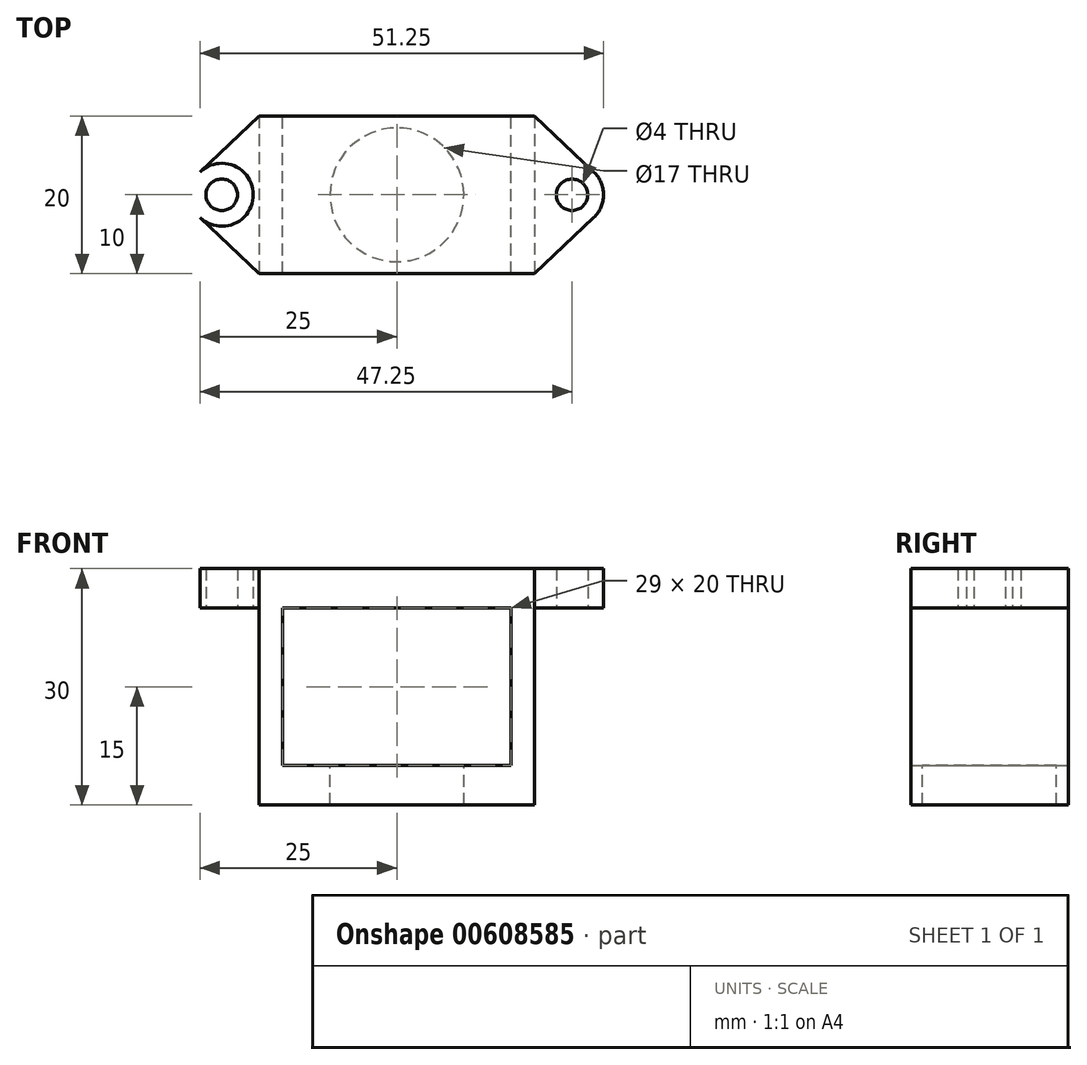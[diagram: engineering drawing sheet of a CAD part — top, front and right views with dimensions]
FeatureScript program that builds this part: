
annotation { "Feature Type Name" : "Feature", "Feature Type Description" : "" }
export const myFeature = defineFeature(function(context is Context, id is Id, definition is map)
    precondition{}
    {
        {
            var Q0;
            Q0=qCreatedBy(makeId("Top.planeOp"),FACE);
            var sketch = newSketch(context, id + "F0", { "sketchPlane" : qUnion([Q0])});
            skLineSegment(sketch, "E0", {"start": v(-22.25, 0) * mm, "end": v(22.25, 0) * mm, "construction": true});
            skCircle(sketch, "E1", {"center": v(22.25, 0) * mm, "radius": 2 * mm});
            skPoint(sketch, "E2", {"position": v(0, 0) * mm});
            skLineSegment(sketch, "E3.bottom", {"start": v(-17.5, 10) * mm, "end": v(17.5, 10) * mm});
            skLineSegment(sketch, "E3.top", {"start": v(-17.5, -10) * mm, "end": v(17.5, -10) * mm});
            skLineSegment(sketch, "E3.left", {"start": v(-17.5, 10) * mm, "end": v(-17.5, -10) * mm});
            skLineSegment(sketch, "E3.right", {"start": v(17.5, 10) * mm, "end": v(17.5, -10) * mm});
            skCircle(sketch, "E4", {"center": v(22.25, 0) * mm, "radius": 4 * mm});
            skLineSegment(sketch, "E5", {"start": v(17.5, -10) * mm, "end": v(25, -2.9) * mm});
            skLineSegment(sketch, "E6", {"start": v(17.5, 10) * mm, "end": v(25, 2.9) * mm});
            skLineSegment(sketch, "E7", {"start": v(0, 0) * mm, "end": v(0, 5.6) * mm, "construction": true});
            skLineSegment(sketch, "E8.MirrorCS", {"start": v(-17.5, 10) * mm, "end": v(-25, 2.9) * mm});
            skCircle(sketch, "E9.MirrorC", {"center": v(-22.25, 0) * mm, "radius": 2 * mm});
            skCircle(sketch, "E10.MirrorC", {"center": v(-22.25, 0) * mm, "radius": 4 * mm});
            skLineSegment(sketch, "E11.MirrorCS", {"start": v(-17.5, -10) * mm, "end": v(-25, -2.9) * mm});
            skLineSegment(sketch, "E12", {"start": v(14.5, -10) * mm, "end": v(14.5, 10) * mm});
            skLineSegment(sketch, "E13.MirrorCS", {"start": v(-14.5, -10) * mm, "end": v(-14.5, 10) * mm});
            skSolve(sketch);
        }
        {
            var Q0;
            Q0=makeQuery(id+"F0.imprint","IMPRINT",FACE,{"disambiguationData":[TD([[makeQuery(id+"F0.imprint","IMPRINT",EDGE,{"derivedFrom":sQuery(id+"F0.wireOp",EDGE,"E3.left")}),-1.0]])]});
            var Q1;
            Q1=makeQuery(id+"F0.imprint","IMPRINT",FACE,{"disambiguationData":[TD([[makeQuery(id+"F0.imprint","IMPRINT",EDGE,{"derivedFrom":sQuery(id+"F0.wireOp",EDGE,"E9.MirrorC")}),1.0]])]});
            var Q2;
            Q2=makeQuery(id+"F0.imprint","IMPRINT",FACE,{"disambiguationData":[TD([[makeQuery(id+"F0.imprint","IMPRINT",EDGE,{"derivedFrom":sQuery(id+"F0.wireOp",EDGE,"E3.bottom")}),-1.0]])]});
            var Q3;
            Q3=makeQuery(id+"F0.imprint","IMPRINT",FACE,{"disambiguationData":[TD([[makeQuery(id+"F0.imprint","IMPRINT",EDGE,{"derivedFrom":sQuery(id+"F0.wireOp",EDGE,"E3.right")}),1.0]])]});
            var Q4;
            Q4=makeQuery(id+"F0.imprint","IMPRINT",FACE,{"disambiguationData":[TD([[makeQuery(id+"F0.imprint","IMPRINT",EDGE,{"derivedFrom":sQuery(id+"F0.wireOp",EDGE,"E1")}),-1.0]])]});
            extrude(context, id + "F1", {"entities" : qUnion([Q0, Q1, Q2, Q3, Q4]), "depth" : 5 * mm, "offsetDistance" : 25 * mm});
        }
        {
            var Q0;
            {var subQ0=sQuery(id+"F0.wireOp",EDGE,"E3.left");Q0=makeQuery(id+"F0.imprint","IMPRINT",FACE,{"disambiguationData":[TD([[makeQuery(id+"F0.imprint","IMPRINT",EDGE,{"derivedFrom":subQ0}),1.0]])]});}
            var Q1;
            {var subQ0=sQuery(id+"F0.wireOp",EDGE,"E3.right");Q1=makeQuery(id+"F0.imprint","IMPRINT",FACE,{"disambiguationData":[TD([[makeQuery(id+"F0.imprint","IMPRINT",EDGE,{"derivedFrom":subQ0}),-1.0]])]});}
            extrude(context, id + "F2", {"entities" : qUnion([Q0, Q1]), "operationType" : NewBodyOperationType.ADD, "oppositeDirection" : true, "depth" : 20 * mm, "offsetDistance" : 25 * mm});
        }
        {
            var Q0;
            Q0=makeQuery(id+"F2.opExtrude","CAP_FACE",FACE,{"disambiguationData":[OSD([sQuery(id+"F0.wireOp",EDGE,"E3.bottom"),sQuery(id+"F0.wireOp",EDGE,"E3.top"),sQuery(id+"F0.wireOp",EDGE,"E3.left"),sQuery(id+"F0.wireOp",EDGE,"E13.MirrorCS")])],"isStart":false});
            var sketch = newSketch(context, id + "F3", { "sketchPlane" : qUnion([Q0])});
            skLineSegment(sketch, "E14.bottom", {"start": v(-17.5, -10) * mm, "end": v(17.5, -10) * mm});
            skLineSegment(sketch, "E14.top", {"start": v(-17.5, 10) * mm, "end": v(17.5, 10) * mm});
            skLineSegment(sketch, "E14.left", {"start": v(-17.5, -10) * mm, "end": v(-17.5, 10) * mm});
            skLineSegment(sketch, "E14.right", {"start": v(17.5, -10) * mm, "end": v(17.5, 10) * mm});
            skCircle(sketch, "E15", {"center": v(0, 0) * mm, "radius": 8.5 * mm});
            skLineSegment(sketch, "E16", {"start": v(17.5, 0) * mm, "end": v(-17.5, 0) * mm, "construction": true});
            skSolve(sketch);
        }
        {
            var Q0;
            {var subQ0=sQuery(id+"F3.wireOp",EDGE,"E14.left");Q0=makeQuery(id+"F3.imprint","IMPRINT",FACE,{"disambiguationData":[TD([[makeQuery(id+"F3.imprint","IMPRINT",EDGE,{"derivedFrom":subQ0}),-1.0]])]});}
            var Q1;
            {var subQ3=sQuery(id+"F3.wireOp",EDGE,"E14.right");Q1=makeQuery(id+"F3.imprint","IMPRINT",FACE,{"disambiguationData":[TD([[makeQuery(id+"F3.imprint","IMPRINT",EDGE,{"derivedFrom":subQ3}),1.0]])]});}
            extrude(context, id + "F4", {"entities" : qUnion([Q0, Q1]), "operationType" : NewBodyOperationType.ADD, "depth" : 5 * mm, "offsetDistance" : 25 * mm});
        }
    });
